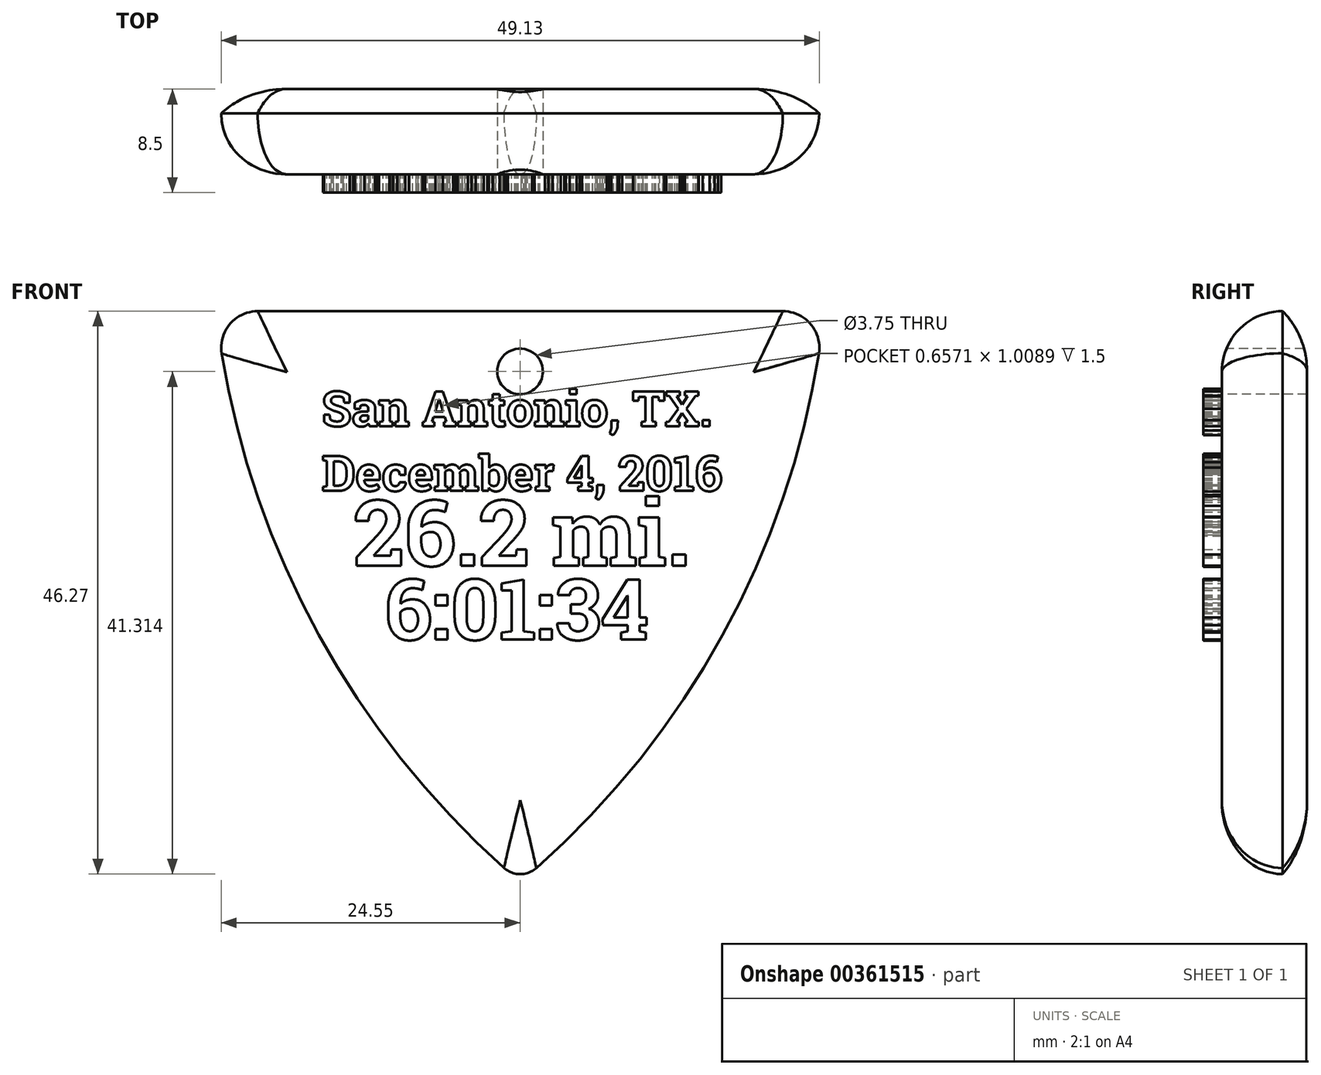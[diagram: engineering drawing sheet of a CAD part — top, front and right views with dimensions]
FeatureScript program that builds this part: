
annotation { "Feature Type Name" : "Feature", "Feature Type Description" : "" }
export const myFeature = defineFeature(function(context is Context, id is Id, definition is map)
    precondition{}
    {
        {
            var Q0;
            Q0=qCreatedBy(makeId("Front.planeOp"),FACE);
            var sketch = newSketch(context, id + "F0", { "sketchPlane" : qUnion([Q0])});
            skLineSegment(sketch, "E0", {"start": v(0, 0) * mm, "end": v(21.58, 0) * mm});
            skLineSegment(sketch, "E1", {"start": v(0, 0) * mm, "end": v(-21.55, 0) * mm});
            skArc(sketch, "E2", {"start": v(-24.51, -3.49) * mm, "mid": v(-16.53, -26.6) * mm, "end": v(-1.33, -45.76) * mm});
            skArc(sketch, "E3", {"start": v(1.33, -45.77) * mm, "mid": v(16.62, -26.64) * mm, "end": v(24.54, -3.47) * mm});
            skPoint(sketch, "E4.visualSharp", {"position": v(-25, 0) * mm});
            skArc(sketch, "E4.filletArc", {"start": v(-21.55, 0) * mm, "mid": v(-23.84, -1.06) * mm, "end": v(-24.51, -3.49) * mm});
            skPoint(sketch, "E5.visualSharp", {"position": v(25, 0) * mm});
            skArc(sketch, "E5.filletArc", {"start": v(24.54, -3.47) * mm, "mid": v(23.86, -1.05) * mm, "end": v(21.58, 0) * mm});
            skPoint(sketch, "E6.visualSharp", {"position": v(0, -46.92) * mm});
            skArc(sketch, "E6.filletArc", {"start": v(-1.33, -45.76) * mm, "mid": v(0, -46.27) * mm, "end": v(1.33, -45.77) * mm});
            skSolve(sketch);
        }
        {
            var Q0;
            Q0 = qSketchRegion(id + "F0", true);
            extrude(context, id + "F1", {"entities" : qUnion([Q0]), "depth" : 7 * mm});
        }
        {
            var Q0;
            Q0=makeQuery(id+"F1.opExtrude","CAP_EDGE",EDGE,{"disambiguationData":[OSD([sQuery(id+"F0.wireOp",EDGE,"E3")])],"isStart":false});
            fillet(context, id + "F2", {"entities" : qUnion([Q0]), "radius" : 5 * mm, "tangentPropagation" : true, "allowEdgeOverflow" : false});
        }
        {
            var Q0;
            Q0=makeQuery(id+"F1.opExtrude","CAP_EDGE",EDGE,{"disambiguationData":[OSD([sQuery(id+"F0.wireOp",EDGE,"E2")])],"isStart":true});
            fillet(context, id + "F3", {"entities" : qUnion([Q0]), "radius" : 7 * mm, "tangentPropagation" : true, "allowEdgeOverflow" : false});
        }
        {
            var Q0;
            Q0=makeQuery(id+"F1.opExtrude","CAP_FACE",FACE,{"disambiguationData":[OSD([sQuery(id+"F0.wireOp",EDGE,"E0"),sQuery(id+"F0.wireOp",EDGE,"E1"),sQuery(id+"F0.wireOp",EDGE,"E2"),sQuery(id+"F0.wireOp",EDGE,"E3"),sQuery(id+"F0.wireOp",EDGE,"E4.filletArc"),sQuery(id+"F0.wireOp",EDGE,"E5.filletArc"),sQuery(id+"F0.wireOp",EDGE,"E6.filletArc")])],"isStart":false});
            var sketch = newSketch(context, id + "F4", { "sketchPlane" : qUnion([Q0])});
            skText(sketch, "E7", { "text": "26.2 mi.", "fontName": "RobotoSlab-Bold.ttf"});
            const initialGuessF4  = {"E7": [-0.01368, -0.02093, 1, 0, 0.00542]};
            skSetInitialGuess(sketch, initialGuessF4);
            skSolve(sketch);
        }
        {
            var Q0;
            Q0 = qSketchRegion(id + "F4", true);
            extrude(context, id + "F5", {"entities" : qUnion([Q0]), "operationType" : NewBodyOperationType.ADD, "depth" : 1.5 * mm});
        }
        {
            var Q0;
            {var subQ0=sQuery(id+"F0.wireOp",EDGE,"E6.filletArc");var subQ1=sQuery(id+"F0.wireOp",EDGE,"E5.filletArc");var subQ2=sQuery(id+"F0.wireOp",EDGE,"E1");var subQ3=sQuery(id+"F0.wireOp",EDGE,"E0");var subQ4=sQuery(id+"F0.wireOp",EDGE,"E2");var subQ5=sQuery(id+"F0.wireOp",EDGE,"E3");var subQ6=sQuery(id+"F0.wireOp",EDGE,"E4.filletArc");Q0=makeQuery(id+"F5.boolean.opBoolean","SPLIT",FACE,{"disambiguationData":[TD([makeQuery(id+"F2.opFillet","BLEND_FACE",FACE,{"disambiguationData":[OSD([subQ4])]})])],"derivedFrom":makeQuery(id+"F1.opExtrude","CAP_FACE",FACE,{"disambiguationData":[OSD([subQ3,subQ2,subQ4,subQ5,subQ6,subQ1,subQ0])],"isStart":false})});}
            var sketch = newSketch(context, id + "F6", { "sketchPlane" : qUnion([Q0])});
            skCircle(sketch, "E8", {"center": v(0, -4.96) * mm, "radius": 1.88 * mm});
            skSolve(sketch);
        }
        {
            var Q0;
            Q0 = qSketchRegion(id + "F6", true);
            extrude(context, id + "F7", {"entities" : qUnion([Q0]), "operationType" : NewBodyOperationType.REMOVE, "oppositeDirection" : true, "depth" : 25 * mm});
        }
        {
            var Q0;
            {var subQ0=sQuery(id+"F0.wireOp",EDGE,"E6.filletArc");var subQ1=sQuery(id+"F0.wireOp",EDGE,"E5.filletArc");var subQ2=sQuery(id+"F0.wireOp",EDGE,"E1");var subQ3=sQuery(id+"F0.wireOp",EDGE,"E0");var subQ4=sQuery(id+"F0.wireOp",EDGE,"E2");var subQ5=sQuery(id+"F0.wireOp",EDGE,"E3");var subQ6=sQuery(id+"F0.wireOp",EDGE,"E4.filletArc");Q0=makeQuery(id+"F5.boolean.opBoolean","SPLIT",FACE,{"disambiguationData":[TD([makeQuery(id+"F2.opFillet","BLEND_FACE",FACE,{"disambiguationData":[OSD([subQ4])]})])],"derivedFrom":makeQuery(id+"F1.opExtrude","CAP_FACE",FACE,{"disambiguationData":[OSD([subQ3,subQ2,subQ4,subQ5,subQ6,subQ1,subQ0])],"isStart":false})});}
            var sketch = newSketch(context, id + "F8", { "sketchPlane" : qUnion([Q0])});
            skText(sketch, "E9", { "text": "San Antonio, TX.\nDecember 4, 2016", "fontName": "RobotoSlab-Bold.ttf"});
            skPoint(sketch, "E10", {"position": v(12.25, -22.61) * mm});
            const initialGuessF8  = {"E9": [-0.01629, -0.00946, 1, 0, 0.0029]};
            skSetInitialGuess(sketch, initialGuessF8);
            skSolve(sketch);
        }
        {
            var Q0;
            Q0 = qSketchRegion(id + "F8", true);
            extrude(context, id + "F9", {"entities" : qUnion([Q0]), "operationType" : NewBodyOperationType.ADD, "depth" : 1.5 * mm});
        }
        {
            var Q0;
            {var subQ51=sQuery(id+"F0.wireOp",EDGE,"E1");var subQ52=sQuery(id+"F0.wireOp",EDGE,"E0");var subQ55=sQuery(id+"F0.wireOp",EDGE,"E4.filletArc");var subQ57=sQuery(id+"F0.wireOp",EDGE,"E3");var subQ59=sQuery(id+"F0.wireOp",EDGE,"E2");var subQ60=makeQuery(id+"F2.opFillet","BLEND_FACE",FACE,{"disambiguationData":[OSD([subQ59])]});var subQ62=sQuery(id+"F0.wireOp",EDGE,"E5.filletArc");var subQ64=sQuery(id+"F0.wireOp",EDGE,"E6.filletArc");Q0=makeQuery(id+"F9.boolean.opBoolean","SPLIT",FACE,{"disambiguationData":[TD([subQ60])],"derivedFrom":makeQuery(id+"F5.boolean.opBoolean","SPLIT",FACE,{"disambiguationData":[TD([subQ60])],"derivedFrom":makeQuery(id+"F1.opExtrude","CAP_FACE",FACE,{"disambiguationData":[OSD([subQ52,subQ51,subQ59,subQ57,subQ55,subQ62,subQ64])],"isStart":false})})});}
            var sketch = newSketch(context, id + "F10", { "sketchPlane" : qUnion([Q0])});
            skText(sketch, "E11", { "text": "6:01:34", "fontName": "RobotoSlab-Bold.ttf"});
            const initialGuessF10  = {"E11": [-0.01113, -0.027, 1, 0, 0.005]};
            skSetInitialGuess(sketch, initialGuessF10);
            skSolve(sketch);
        }
        {
            var Q0;
            Q0 = qSketchRegion(id + "F10", true);
            extrude(context, id + "F11", {"entities" : qUnion([Q0]), "operationType" : NewBodyOperationType.ADD, "depth" : 1.5 * mm});
        }
    });
